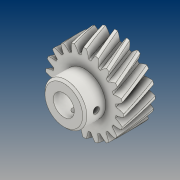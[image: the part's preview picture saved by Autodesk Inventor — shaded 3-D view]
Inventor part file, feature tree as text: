
AUTODESK INVENTOR PART (.ipt)
format: ipt  version: 2021 (Build 250183000, 183)  size: 446,464 bytes
history: native  units: mm (DEFAULTED — no unit token found)
features: extrude x4, sketch x4, plane x3, other x3, chamfer x1, pattern_circular x1, projected_geometry x1
ambient origin geometry x8: Origin, YZ Plane, XZ Plane, XY Plane, X Axis, Y Axis, Z Axis, Center Point
bodies: Solid1 (feature_tree)
feature tree (17):
  extrude  "Extrusion1"  Depth=15.0mm TaperAngle=0.0deg
  plane  "Work Plane2"
  plane  "Work Plane8"
  plane  "Work Plane9"
  other  "Spur Gear"
  sketch  "Sketch3"  dims[d16=60.0mm d17=0.0mm d34=1.570796mm]
  extrude  "Extrusion2"  Depth=10.0mm TaperAngle=0.0deg
  extrude  "Extrusion3"  Depth=1.570796mm TaperAngle=0.0deg
  chamfer  "Chamfer1"  [1 undecoded]
  extrude  "Extrusion4"  Depth=10.0mm
  pattern_circular  "Circular Pattern1"  Count=6  [1 undecoded]
  sketch  "Sketch1"  dims[d0=37.237438mm d1=15.0mm d2=0.0mm]
  sketch  "Sketch2"  dims[d3=34.053689mm d4=10.0mm d5=0.0mm]
  other  "Srf1"
  sketch  "Sketch4"  dims[d39=0.0mm d41=0.0mm d43=60.0mm d46=60.0mm d47=0.0mm d48=0.0mm d49=10.0mm d50=5.0mm d51=10.0mm d52=0.0mm d53=30.25mm d54=0.0mm d55=1.0mm d56=2.0mm d57=45.0deg d58=3.0mm d59=30.25mm d60=0.0mm d61=20.0mm d62=90.0deg]
  projected_geometry  "Projected Loop1"
  other  "Pitch Diameter"
note: 2 required parameter values undecoded (feature->parameter linkage not recoverable at this tier; creation-order binding heuristic only, values carry confidence <= 0.55)
